# Revit family: GSY-E40
name_source: partatom
category: Structural Framing
revit_build: Autodesk Revit 2018 (Build: 20190510_1515(x64)
units: mm (PartAtom-declared; Revit-internal decimal feet)

## family parameters
Always export as geometry = No
Always vertical = Yes
Cut with Voids When Loaded = No
Material for Model Behavior = Other
OmniClass Number = 23.25.30.11.14.14
OmniClass Title = Beams
Section Shape = Not Defined
Shared = No
Show family pre-cut in plan views = Yes

## types (5) — shared parameters
Manufacturer = Give Steel A/S
d = 15 mm  [stored 0.0492126 ft]
hw = 360 mm  [stored 1.1811 ft]
t1 = 40 mm  [stored 0.131234 ft]
t2 = 25 mm  [stored 0.082021 ft]

## per-type parameters (varying)
| type | b1 | b2 |
| GSY-E40/15-34 | 150 mm | 340 mm  [stored 1.11549 ft] |
| GSY-E40/18-37 | 180 mm  [stored 0.590551 ft] | 370 mm  [stored 1.21391 ft] |
| GSY-E40/22-41 | 220 mm  [stored 0.721785 ft] | 410 mm  [stored 1.34514 ft] |
| GSY-E40/27-46 | 270 mm  [stored 0.885827 ft] | 460 mm  [stored 1.50919 ft] |
| GSY-E40/30-49 | 300 mm | 490 mm  [stored 1.60761 ft] |

note: [stored X ft] marks values corroborated as IEEE doubles in the binary element streams (Revit-internal decimal feet)

## geometry (parser evidence)
native form markers: Sweep x3
no freeform markers — native parametric forms only
